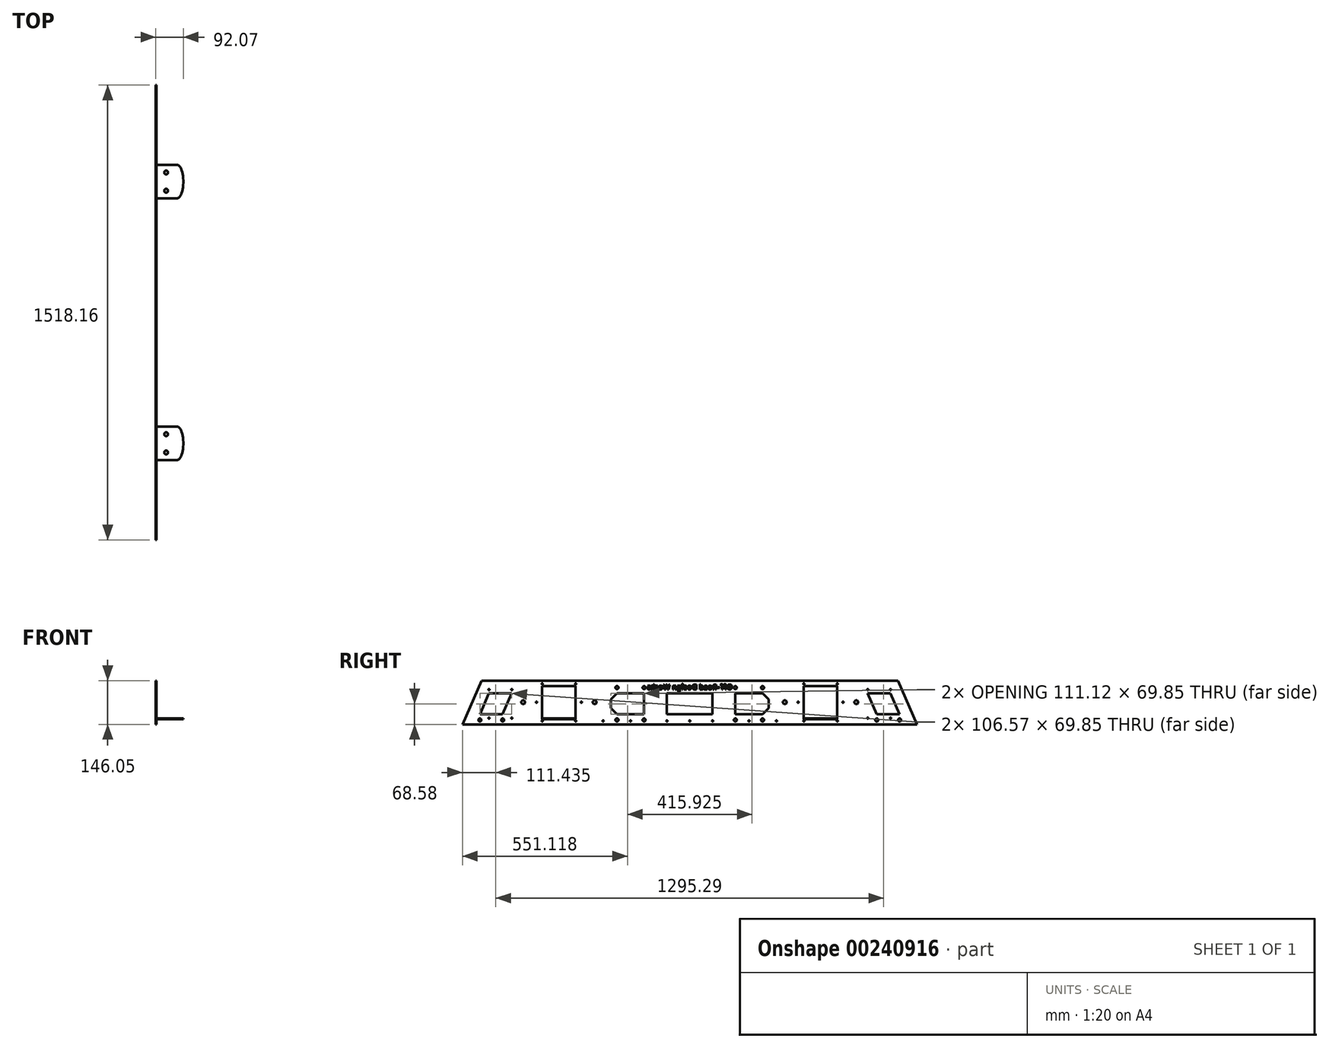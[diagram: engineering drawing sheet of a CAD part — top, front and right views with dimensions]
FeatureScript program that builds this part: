
annotation { "Feature Type Name" : "Feature", "Feature Type Description" : "" }
export const myFeature = defineFeature(function(context is Context, id is Id, definition is map)
    precondition{}
    {
        {
            var Q0;
            Q0=qCreatedBy(makeId("Right.planeOp"),FACE);
            var sketch = newSketch(context, id + "F0", { "sketchPlane" : qUnion([Q0])});
            skLineSegment(sketch, "E0", {"start": v(0, 0) * mm, "end": v(-759.08, 0) * mm});
            skLineSegment(sketch, "E1", {"start": v(-759.08, 0) * mm, "end": v(-695.58, 146.05) * mm});
            skLineSegment(sketch, "E2", {"start": v(-695.58, 146.05) * mm, "end": v(0, 146.05) * mm});
            skLineSegment(sketch, "E3", {"start": v(0, 0) * mm, "end": v(0, 460.36) * mm, "construction": true});
            skLineSegment(sketch, "E4.MirrorCS", {"start": v(695.58, 146.05) * mm, "end": v(0, 146.05) * mm});
            skLineSegment(sketch, "E5.MirrorCS", {"start": v(759.08, 0) * mm, "end": v(695.58, 146.05) * mm});
            skLineSegment(sketch, "E6.MirrorCS", {"start": v(0, 0) * mm, "end": v(759.08, 0) * mm});
            skSolve(sketch);
        }
        {
            var Q0;
            Q0=qSketchRegion(id+"F0",true);
            extrude(context, id + "F1", {"entities" : qUnion([Q0]), "oppositeDirection" : true, "depth" : 3.17 * mm});
        }
        {
            var Q0;
            Q0=makeQuery(id+"F1.opExtrude","CAP_FACE",FACE,{"disambiguationData":[OSD([sQuery(id+"F0.wireOp",EDGE,"E0"),sQuery(id+"F0.wireOp",EDGE,"E1"),sQuery(id+"F0.wireOp",EDGE,"E2"),sQuery(id+"F0.wireOp",EDGE,"E4.MirrorCS"),sQuery(id+"F0.wireOp",EDGE,"E5.MirrorCS"),sQuery(id+"F0.wireOp",EDGE,"E6.MirrorCS")])],"isStart":true});
            var sketch = newSketch(context, id + "F2", { "sketchPlane" : qUnion([Q0])});
            skLineSegment(sketch, "E7", {"start": v(0, 0) * mm, "end": v(0, 457.35) * mm, "construction": true});
            skLineSegment(sketch, "E8.bottom", {"start": v(-492.76, 127.5) * mm, "end": v(-381, 127.5) * mm});
            skLineSegment(sketch, "E8.top", {"start": v(-492.76, 20.32) * mm, "end": v(-381, 20.32) * mm});
            skLineSegment(sketch, "E8.left", {"start": v(-492.76, 127.5) * mm, "end": v(-492.76, 20.32) * mm});
            skLineSegment(sketch, "E8.right", {"start": v(-381, 127.5) * mm, "end": v(-381, 20.32) * mm});
            skLineSegment(sketch, "E9", {"start": v(-594.36, 103.5) * mm, "end": v(-670.56, 103.5) * mm});
            skLineSegment(sketch, "E10", {"start": v(-670.56, 103.5) * mm, "end": v(-700.93, 33.65) * mm});
            skLineSegment(sketch, "E11", {"start": v(-700.93, 33.65) * mm, "end": v(-624.73, 33.65) * mm});
            skLineSegment(sketch, "E12", {"start": v(-624.73, 33.65) * mm, "end": v(-594.36, 103.5) * mm});
            skArc(sketch, "E13.cCircle", {"start": v(-228.6, 103.5) * mm, "mid": v(-263.53, 68.58) * mm, "end": v(-228.6, 33.65) * mm, "construction": true});
            skLineSegment(sketch, "E13.0", {"start": v(-243.07, 103.5) * mm, "end": v(-214.13, 103.5) * mm});
            skLineSegment(sketch, "E13.4", {"start": v(-214.13, 33.65) * mm, "end": v(-243.07, 33.65) * mm});
            skLineSegment(sketch, "E13.5", {"start": v(-243.07, 33.65) * mm, "end": v(-263.53, 54.11) * mm});
            skLineSegment(sketch, "E13.6", {"start": v(-263.53, 54.11) * mm, "end": v(-263.53, 83.05) * mm});
            skLineSegment(sketch, "E13.7", {"start": v(-263.53, 83.05) * mm, "end": v(-243.07, 103.5) * mm});
            skPoint(sketch, "E13.0.midPoint", {"position": v(-228.6, 103.5) * mm});
            skLineSegment(sketch, "E14", {"start": v(-228.6, 33.65) * mm, "end": v(-152.4, 33.65) * mm});
            skLineSegment(sketch, "E15.MirrorCS", {"start": v(492.76, 127.5) * mm, "end": v(381, 127.5) * mm});
            skLineSegment(sketch, "E16.MirrorCS", {"start": v(492.76, 20.32) * mm, "end": v(381, 20.32) * mm});
            skLineSegment(sketch, "E17.MirrorCS", {"start": v(492.76, 127.5) * mm, "end": v(492.76, 20.32) * mm});
            skLineSegment(sketch, "E18.MirrorCS", {"start": v(381, 127.5) * mm, "end": v(381, 20.32) * mm});
            skLineSegment(sketch, "E19.MirrorCS", {"start": v(594.36, 103.5) * mm, "end": v(670.56, 103.5) * mm});
            skLineSegment(sketch, "E20.MirrorCS", {"start": v(670.56, 103.5) * mm, "end": v(700.93, 33.66) * mm});
            skLineSegment(sketch, "E21.MirrorCS", {"start": v(700.93, 33.65) * mm, "end": v(624.73, 33.65) * mm});
            skLineSegment(sketch, "E22.MirrorCS", {"start": v(624.73, 33.65) * mm, "end": v(594.36, 103.5) * mm});
            skLineSegment(sketch, "E23.MirrorCS", {"start": v(263.53, 54.11) * mm, "end": v(263.53, 83.05) * mm});
            skLineSegment(sketch, "E24.MirrorCS", {"start": v(263.53, 83.05) * mm, "end": v(243.07, 103.5) * mm});
            skArc(sketch, "E25.MirrorCS", {"start": v(228.6, 103.5) * mm, "mid": v(263.53, 68.58) * mm, "end": v(228.6, 33.65) * mm, "construction": true});
            skLineSegment(sketch, "E26.MirrorCS", {"start": v(243.07, 33.65) * mm, "end": v(263.53, 54.11) * mm});
            skLineSegment(sketch, "E27.MirrorCS", {"start": v(214.13, 33.65) * mm, "end": v(243.07, 33.65) * mm});
            skLineSegment(sketch, "E28.MirrorCS", {"start": v(243.07, 103.5) * mm, "end": v(214.13, 103.5) * mm});
            skLineSegment(sketch, "E29.MirrorCS", {"start": v(0, 103.5) * mm, "end": v(76.2, 103.5) * mm});
            skLineSegment(sketch, "E30.MirrorCS", {"start": v(228.6, 33.65) * mm, "end": v(152.4, 33.65) * mm});
            skLineSegment(sketch, "E31", {"start": v(-114.3, 103.5) * mm, "end": v(-114.3, -30.3) * mm, "construction": true});
            skLineSegment(sketch, "E32", {"start": v(-152.4, 103.5) * mm, "end": v(-152.4, 33.65) * mm});
            skLineSegment(sketch, "E33.MirrorCS", {"start": v(-76.2, 103.5) * mm, "end": v(-76.2, 33.65) * mm});
            skLineSegment(sketch, "E34.trimOffspring", {"start": v(-152.4, 103.5) * mm, "end": v(-228.6, 103.5) * mm});
            skPoint(sketch, "E35.start.orphan", {"position": v(0, 103.5) * mm});
            skLineSegment(sketch, "E36.trimOffspring", {"start": v(-76.2, 33.65) * mm, "end": v(0, 33.65) * mm});
            skLineSegment(sketch, "E37", {"start": v(-76.2, 103.5) * mm, "end": v(0, 103.5) * mm});
            skLineSegment(sketch, "E38", {"start": v(114.3, 103.5) * mm, "end": v(114.3, -63.26) * mm, "construction": true});
            skPoint(sketch, "E38.endSnap0", {"position": v(114.3, 103.5) * mm});
            skLineSegment(sketch, "E39", {"start": v(152.4, 103.5) * mm, "end": v(152.4, 33.65) * mm});
            skLineSegment(sketch, "E40.MirrorCS", {"start": v(76.2, 103.5) * mm, "end": v(76.2, 33.65) * mm});
            skLineSegment(sketch, "E41.trimOffspring", {"start": v(152.4, 103.5) * mm, "end": v(228.6, 103.5) * mm});
            skLineSegment(sketch, "E42.trimOffspring", {"start": v(76.2, 33.65) * mm, "end": v(0, 33.65) * mm});
            skSolve(sketch);
        }
        {
            var Q0;
            Q0=qSketchRegion(id+"F2",true);
            var Q1;
            Q1=makeQuery(id+"F1.opExtrude","CAP_FACE",FACE,{"disambiguationData":[OSD([sQuery(id+"F0.wireOp",EDGE,"E0"),sQuery(id+"F0.wireOp",EDGE,"E1"),sQuery(id+"F0.wireOp",EDGE,"E2"),sQuery(id+"F0.wireOp",EDGE,"E4.MirrorCS"),sQuery(id+"F0.wireOp",EDGE,"E5.MirrorCS"),sQuery(id+"F0.wireOp",EDGE,"E6.MirrorCS")])],"isStart":false});
            extrude(context, id + "F3", {"entities" : qUnion([Q0]), "operationType" : NewBodyOperationType.REMOVE, "endBound" : BoundingType.UP_TO_SURFACE, "oppositeDirection" : true, "endBoundEntityFace" : qUnion([Q1]), "depth" : 25.4 * mm});
        }
        {
            var Q0;
            Q0=makeQuery(id+"F1.opExtrude","CAP_FACE",FACE,{"disambiguationData":[OSD([sQuery(id+"F0.wireOp",EDGE,"E0"),sQuery(id+"F0.wireOp",EDGE,"E1"),sQuery(id+"F0.wireOp",EDGE,"E2"),sQuery(id+"F0.wireOp",EDGE,"E4.MirrorCS"),sQuery(id+"F0.wireOp",EDGE,"E5.MirrorCS"),sQuery(id+"F0.wireOp",EDGE,"E6.MirrorCS")])],"isStart":true});
            var sketch = newSketch(context, id + "F4", { "sketchPlane" : qUnion([Q0])});
            skCircle(sketch, "E43", {"center": v(-670.56, 116.2) * mm, "radius": 1.9 * mm});
            skCircle(sketch, "E44", {"center": v(-594.36, 116.2) * mm, "radius": 1.9 * mm});
            skCircle(sketch, "E45", {"center": v(-670.56, 20.95) * mm, "radius": 1.9 * mm});
            skCircle(sketch, "E46", {"center": v(-594.36, 20.95) * mm, "radius": 1.9 * mm});
            skCircle(sketch, "E47", {"center": v(-624.73, 14.6) * mm, "radius": 5.08 * mm});
            skCircle(sketch, "E48", {"center": v(-700.93, 14.6) * mm, "radius": 5.08 * mm});
            skCircle(sketch, "E49", {"center": v(-492.76, 135.13) * mm, "radius": 1.9 * mm});
            skCircle(sketch, "E50", {"center": v(-381, 135.13) * mm, "radius": 1.9 * mm});
            skLineSegment(sketch, "E51", {"start": v(-492.76, 73.91) * mm, "end": v(-416.14, 73.91) * mm, "construction": true});
            skCircle(sketch, "E52", {"center": v(-492.76, 11.43) * mm, "radius": 1.9 * mm});
            skCircle(sketch, "E53", {"center": v(-381, 11.43) * mm, "radius": 1.9 * mm});
            skCircle(sketch, "E54", {"center": v(-243.07, 14.6) * mm, "radius": 5.08 * mm});
            skCircle(sketch, "E55", {"center": v(-152.4, 14.6) * mm, "radius": 5.08 * mm});
            skLineSegment(sketch, "E56", {"start": v(-263.53, 68.58) * mm, "end": v(-277.88, 68.58) * mm, "construction": true});
            skCircle(sketch, "E57.MirrorC", {"center": v(-243.07, 122.56) * mm, "radius": 5.08 * mm});
            skCircle(sketch, "E58.MirrorC", {"center": v(-152.4, 122.56) * mm, "radius": 5.08 * mm});
            skLineSegment(sketch, "E59", {"start": v(0, 0) * mm, "end": v(0, -131.47) * mm, "construction": true});
            skCircle(sketch, "E60.MirrorC", {"center": v(152.4, 122.56) * mm, "radius": 5.08 * mm});
            skCircle(sketch, "E61.MirrorC", {"center": v(243.07, 122.56) * mm, "radius": 5.08 * mm});
            skCircle(sketch, "E62.MirrorC", {"center": v(243.07, 14.6) * mm, "radius": 5.08 * mm});
            skCircle(sketch, "E63.MirrorC", {"center": v(152.4, 14.6) * mm, "radius": 5.08 * mm});
            skCircle(sketch, "E64.MirrorC", {"center": v(381, 11.43) * mm, "radius": 1.9 * mm});
            skCircle(sketch, "E65.MirrorC", {"center": v(492.76, 11.43) * mm, "radius": 1.9 * mm});
            skCircle(sketch, "E66.MirrorC", {"center": v(492.76, 135.13) * mm, "radius": 1.9 * mm});
            skCircle(sketch, "E67.MirrorC", {"center": v(381, 135.13) * mm, "radius": 1.9 * mm});
            skCircle(sketch, "E68.MirrorC", {"center": v(594.36, 116.2) * mm, "radius": 1.9 * mm});
            skCircle(sketch, "E69.MirrorC", {"center": v(670.56, 116.2) * mm, "radius": 1.9 * mm});
            skCircle(sketch, "E70.MirrorC", {"center": v(670.56, 20.95) * mm, "radius": 1.9 * mm});
            skCircle(sketch, "E71.MirrorC", {"center": v(594.36, 20.95) * mm, "radius": 1.9 * mm});
            skCircle(sketch, "E72.MirrorC", {"center": v(624.73, 14.6) * mm, "radius": 5.08 * mm});
            skCircle(sketch, "E73.MirrorC", {"center": v(700.93, 14.6) * mm, "radius": 5.08 * mm});
            skCircle(sketch, "E74", {"center": v(-361.95, 73.91) * mm, "radius": 1.9 * mm});
            skPoint(sketch, "E74.centerSnap0", {"position": v(-381, 73.91) * mm});
            skCircle(sketch, "E75", {"center": v(-511.81, 73.91) * mm, "radius": 1.9 * mm});
            skCircle(sketch, "E76.MirrorC", {"center": v(361.95, 73.91) * mm, "radius": 1.9 * mm});
            skCircle(sketch, "E77.MirrorC", {"center": v(511.81, 73.91) * mm, "radius": 1.9 * mm});
            skCircle(sketch, "E78", {"center": v(-197.73, 11.43) * mm, "radius": 1.9 * mm});
            skPoint(sketch, "E78.centerSnap0", {"position": v(-197.73, 33.66) * mm});
            skCircle(sketch, "E79", {"center": v(-289.37, 11.43) * mm, "radius": 1.9 * mm});
            skCircle(sketch, "E80.MirrorC", {"center": v(197.73, 11.43) * mm, "radius": 1.9 * mm});
            skCircle(sketch, "E81.MirrorC", {"center": v(289.37, 11.43) * mm, "radius": 1.9 * mm});
            skCircle(sketch, "E82", {"center": v(-76.2, 11.43) * mm, "radius": 1.9 * mm});
            skCircle(sketch, "E83", {"center": v(0, 11.43) * mm, "radius": 1.9 * mm});
            skPoint(sketch, "E83.centerSnap0", {"position": v(0, 33.66) * mm});
            skCircle(sketch, "E84", {"center": v(76.2, 11.43) * mm, "radius": 1.9 * mm});
            skCircle(sketch, "E85", {"center": v(-317.5, 73.91) * mm, "radius": 6.35 * mm});
            skCircle(sketch, "E86", {"center": v(-556.26, 73.91) * mm, "radius": 6.35 * mm});
            skCircle(sketch, "E87.MirrorC", {"center": v(317.5, 73.91) * mm, "radius": 6.35 * mm});
            skCircle(sketch, "E88.MirrorC", {"center": v(556.26, 73.91) * mm, "radius": 6.35 * mm});
            skSolve(sketch);
        }
        {
            var Q0;
            Q0=qSketchRegion(id+"F4",true);
            var Q1;
            Q1=makeQuery(id+"F1.opExtrude","CAP_FACE",FACE,{"disambiguationData":[OSD([sQuery(id+"F0.wireOp",EDGE,"E0"),sQuery(id+"F0.wireOp",EDGE,"E1"),sQuery(id+"F0.wireOp",EDGE,"E2"),sQuery(id+"F0.wireOp",EDGE,"E4.MirrorCS"),sQuery(id+"F0.wireOp",EDGE,"E5.MirrorCS"),sQuery(id+"F0.wireOp",EDGE,"E6.MirrorCS")])],"isStart":false});
            extrude(context, id + "F5", {"entities" : qUnion([Q0]), "operationType" : NewBodyOperationType.REMOVE, "endBound" : BoundingType.UP_TO_SURFACE, "oppositeDirection" : true, "endBoundEntityFace" : qUnion([Q1]), "depth" : 25.4 * mm});
        }
        {
            var Q0;
            Q0=makeQuery(id+"F3.boolean.opBoolean","COPY",FACE,{"derivedFrom":makeQuery(id+"F3.opExtrude","SWEPT_FACE",FACE,{"disambiguationData":[OSD([sQuery(id+"F2.wireOp",EDGE,"E8.top")])]})});
            var sketch = newSketch(context, id + "F6", { "sketchPlane" : qUnion([Q0])});
            skLineSegment(sketch, "E89", {"start": v(-3.18, -436.88) * mm, "end": v(-45.3, -436.88) * mm, "construction": true});
            skLineSegment(sketch, "E90", {"start": v(-3.18, -492.76) * mm, "end": v(-71.76, -492.76) * mm});
            skLineSegment(sketch, "E91.MirrorCS", {"start": v(-3.18, -381) * mm, "end": v(-71.76, -381) * mm});
            skEllipticalArc(sketch, "E92", {});
            skLineSegment(sketch, "E93", {"start": v(-3.18, -492.76) * mm, "end": v(-3.18, -381) * mm});
            skCircle(sketch, "E94", {"center": v(-34.93, -467.36) * mm, "radius": 6.35 * mm});
            skCircle(sketch, "E95.MirrorC", {"center": v(-34.93, -406.4) * mm, "radius": 6.35 * mm});
            skLineSegment(sketch, "E96", {"start": v(0, 0) * mm, "end": v(-238.43, 0) * mm, "construction": true});
            skLineSegment(sketch, "E97.MirrorCS", {"start": v(-3.18, 381) * mm, "end": v(-71.76, 381) * mm});
            skEllipticalArc(sketch, "E98.MirrorCS", {});
            skCircle(sketch, "E99.MirrorC", {"center": v(-34.93, 406.4) * mm, "radius": 6.35 * mm});
            skCircle(sketch, "E100.MirrorC", {"center": v(-34.93, 467.36) * mm, "radius": 6.35 * mm});
            skLineSegment(sketch, "E101.MirrorCS", {"start": v(-3.18, 492.76) * mm, "end": v(-71.76, 492.76) * mm});
            skLineSegment(sketch, "E102.MirrorCS", {"start": v(-3.18, 492.76) * mm, "end": v(-3.18, 381) * mm});
            const initialGuessF6  = {"E92": [-0.071755, -0.43688, 0, -1, 0.05588, 0.02032, 3.141592653589793, 0], "E98.MirrorCS": [-0.071755, 0.43688, 0, 1, 0.05588, 0.02032, 0, 3.141592653589793]};
            skSetInitialGuess(sketch, initialGuessF6);
            skSolve(sketch);
        }
        {
            var Q0;
            Q0=qSketchRegion(id+"F6",true);
            extrude(context, id + "F7", {"entities" : qUnion([Q0]), "operationType" : NewBodyOperationType.ADD, "oppositeDirection" : true, "depth" : 3.17 * mm});
        }
        {
            var Q0;
            Q0=makeQuery(id+"F1.opExtrude","SWEPT_BODY",BODY,{"disambiguationData":[OSD([sQuery(id+"F0.wireOp",EDGE,"E0"),sQuery(id+"F0.wireOp",EDGE,"E1"),sQuery(id+"F0.wireOp",EDGE,"E2"),sQuery(id+"F0.wireOp",EDGE,"E4.MirrorCS"),sQuery(id+"F0.wireOp",EDGE,"E5.MirrorCS"),sQuery(id+"F0.wireOp",EDGE,"E6.MirrorCS")])]});
            var Q1;
            Q1=qCreatedBy(makeId("Right.planeOp"),FACE);
            mirror(context, id + "F8", {"entities" : qUnion([Q0]), "mirrorPlane" : qUnion([Q1])});
        }
        {
            var Q0;
            Q0=makeQuery(id+"F1.opExtrude","SWEPT_BODY",BODY,{"disambiguationData":[OSD([sQuery(id+"F0.wireOp",EDGE,"E0"),sQuery(id+"F0.wireOp",EDGE,"E1"),sQuery(id+"F0.wireOp",EDGE,"E2"),sQuery(id+"F0.wireOp",EDGE,"E4.MirrorCS"),sQuery(id+"F0.wireOp",EDGE,"E5.MirrorCS"),sQuery(id+"F0.wireOp",EDGE,"E6.MirrorCS")])]});
            deleteBodies(context, id + "F9", {"entities" : qUnion([Q0])});
        }
        {
            var Q0;
            Q0=makeQuery(id+"F8.opPattern","COPY",FACE,{"derivedFrom":makeQuery(id+"F1.opExtrude","CAP_FACE",FACE,{"disambiguationData":[OSD([sQuery(id+"F0.wireOp",EDGE,"E0"),sQuery(id+"F0.wireOp",EDGE,"E1"),sQuery(id+"F0.wireOp",EDGE,"E2"),sQuery(id+"F0.wireOp",EDGE,"E4.MirrorCS"),sQuery(id+"F0.wireOp",EDGE,"E5.MirrorCS"),sQuery(id+"F0.wireOp",EDGE,"E6.MirrorCS")])],"isStart":true}),"instanceName":"1"});
            var sketch = newSketch(context, id + "F10", { "sketchPlane" : qUnion([Q0])});
            skText(sketch, "E103", { "text": "Off-Road Design Works", "fontName": "AllertaStencil-Regular.ttf"});
            skLineSegment(sketch, "E104", {"start": v(0, 116.2) * mm, "end": v(0, 0) * mm, "construction": true});
            const initialGuessF10  = {"E103": [-0.14224, 0.1162, 1, 0, 0.01718]};
            skSetInitialGuess(sketch, initialGuessF10);
            skSolve(sketch);
        }
        {
            var Q0;
            Q0=qSketchRegion(id+"F10",true);
            var Q1;
            Q1=makeQuery(id+"F8.opPattern","COPY",FACE,{"derivedFrom":makeQuery(id+"F1.opExtrude","CAP_FACE",FACE,{"disambiguationData":[OSD([sQuery(id+"F0.wireOp",EDGE,"E0"),sQuery(id+"F0.wireOp",EDGE,"E1"),sQuery(id+"F0.wireOp",EDGE,"E2"),sQuery(id+"F0.wireOp",EDGE,"E4.MirrorCS"),sQuery(id+"F0.wireOp",EDGE,"E5.MirrorCS"),sQuery(id+"F0.wireOp",EDGE,"E6.MirrorCS")])],"isStart":false}),"instanceName":"1"});
            extrude(context, id + "F11", {"entities" : qUnion([Q0]), "operationType" : NewBodyOperationType.REMOVE, "endBound" : BoundingType.UP_TO_SURFACE, "oppositeDirection" : true, "endBoundEntityFace" : qUnion([Q1]), "depth" : 25.4 * mm});
        }
    });
